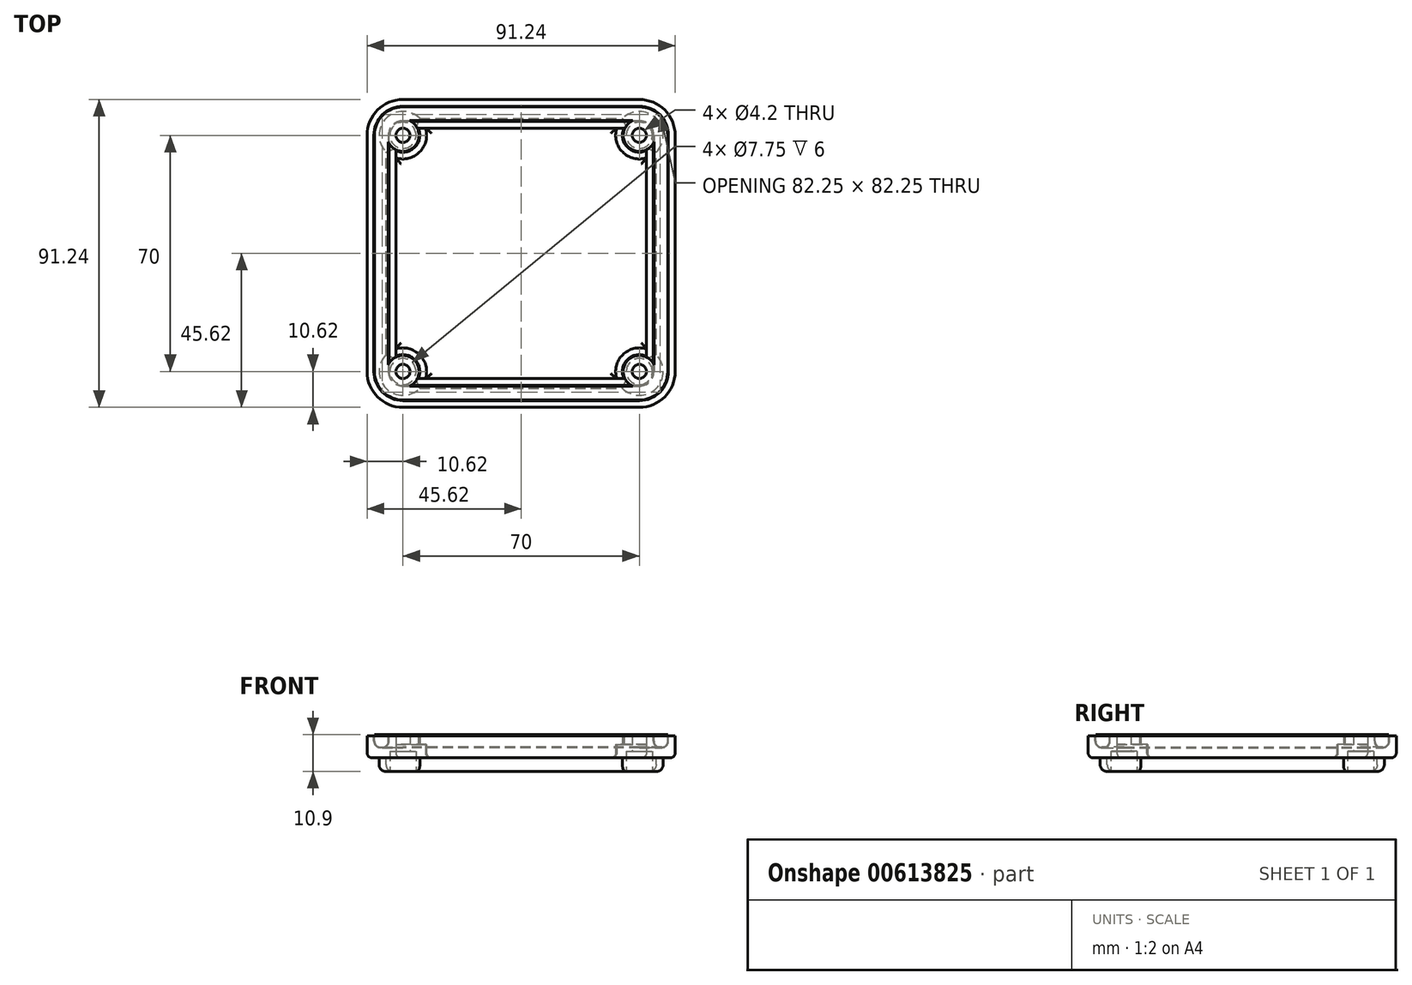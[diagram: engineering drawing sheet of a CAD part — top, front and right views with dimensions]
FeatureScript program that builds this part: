
annotation { "Feature Type Name" : "Feature", "Feature Type Description" : "" }
export const myFeature = defineFeature(function(context is Context, id is Id, definition is map)
    precondition{}
    {
        {
            var Q0;
            Q0=qCreatedBy(makeId("Top.planeOp"),FACE);
            var sketch = newSketch(context, id + "F0", { "sketchPlane" : qUnion([Q0])});
            skLineSegment(sketch, "E0.bottom", {"start": v(35, -45.63) * mm, "end": v(-35, -45.63) * mm});
            skLineSegment(sketch, "E0.top", {"start": v(35, 45.63) * mm, "end": v(-35, 45.63) * mm});
            skLineSegment(sketch, "E0.left", {"start": v(45.62, -35) * mm, "end": v(45.62, 35) * mm});
            skLineSegment(sketch, "E0.right", {"start": v(-45.62, -35) * mm, "end": v(-45.62, 35) * mm});
            skPoint(sketch, "E0.middle", {"position": v(0, 0) * mm});
            skPoint(sketch, "E1.visualSharp", {"position": v(-45.62, 45.62) * mm});
            skArc(sketch, "E1.filletArc", {"start": v(-35, 45.63) * mm, "mid": v(-42.51, 42.51) * mm, "end": v(-45.63, 35) * mm});
            skPoint(sketch, "E2.visualSharp", {"position": v(45.62, 45.63) * mm});
            skArc(sketch, "E2.filletArc", {"start": v(45.62, 35) * mm, "mid": v(42.51, 42.51) * mm, "end": v(35, 45.63) * mm});
            skPoint(sketch, "E3.visualSharp", {"position": v(45.62, -45.62) * mm});
            skArc(sketch, "E3.filletArc", {"start": v(35, -45.63) * mm, "mid": v(42.51, -42.51) * mm, "end": v(45.62, -35) * mm});
            skPoint(sketch, "E4.visualSharp", {"position": v(-45.62, -45.63) * mm});
            skArc(sketch, "E4.filletArc", {"start": v(-45.62, -35) * mm, "mid": v(-42.51, -42.51) * mm, "end": v(-35, -45.63) * mm});
            skLineSegment(sketch, "E5.bottom", {"start": v(-35, 35) * mm, "end": v(35, 35) * mm, "construction": true});
            skLineSegment(sketch, "E5.top", {"start": v(-35, -35) * mm, "end": v(35, -35) * mm, "construction": true});
            skLineSegment(sketch, "E5.left", {"start": v(-35, 35) * mm, "end": v(-35, -35) * mm, "construction": true});
            skLineSegment(sketch, "E5.right", {"start": v(35, 35) * mm, "end": v(35, -35) * mm, "construction": true});
            skCircle(sketch, "E6", {"center": v(-35, 35) * mm, "radius": 2.1 * mm});
            skCircle(sketch, "E7", {"center": v(35, 35) * mm, "radius": 2.1 * mm});
            skCircle(sketch, "E8", {"center": v(35, -35) * mm, "radius": 2.1 * mm});
            skCircle(sketch, "E9", {"center": v(-35, -35) * mm, "radius": 2.1 * mm});
            skLineSegment(sketch, "E10", {"start": v(-30.46, 37.1) * mm, "end": v(30.46, 37.1) * mm});
            skLineSegment(sketch, "E11", {"start": v(-37.1, 30.46) * mm, "end": v(-37.1, -30.46) * mm});
            skLineSegment(sketch, "E12", {"start": v(-30.46, -37.1) * mm, "end": v(30.46, -37.1) * mm});
            skLineSegment(sketch, "E13", {"start": v(37.1, -30.46) * mm, "end": v(37.1, 30.46) * mm});
            skArc(sketch, "E14", {"start": v(30.46, 37.1) * mm, "mid": v(31.46, 31.46) * mm, "end": v(37.1, 30.46) * mm});
            skArc(sketch, "E15", {"start": v(-37.1, 30.46) * mm, "mid": v(-31.46, 31.46) * mm, "end": v(-30.46, 37.1) * mm});
            skArc(sketch, "E16", {"start": v(-30.46, -37.1) * mm, "mid": v(-31.46, -31.46) * mm, "end": v(-37.1, -30.46) * mm});
            skArc(sketch, "E17", {"start": v(37.1, -30.46) * mm, "mid": v(31.46, -31.46) * mm, "end": v(30.46, -37.1) * mm});
            skPoint(sketch, "E18.orphan", {"position": v(-37.1, 35) * mm});
            skPoint(sketch, "E19.orphan", {"position": v(-35, 37.1) * mm});
            skPoint(sketch, "E20.orphan", {"position": v(37.1, 35) * mm});
            skPoint(sketch, "E21.orphan", {"position": v(37.1, -35) * mm});
            skPoint(sketch, "E22.orphan", {"position": v(35, -37.1) * mm});
            skPoint(sketch, "E23.orphan", {"position": v(-37.1, -35) * mm});
            skPoint(sketch, "E24.orphan", {"position": v(-35, -37.1) * mm});
            skSolve(sketch);
        }
        {
            var Q0;
            Q0 = qSketchRegion(id + "F0", true);
            extrude(context, id + "F1", {"entities" : qUnion([Q0]), "depth" : 6.5 * mm, "offsetDistance" : 25 * mm});
        }
        {
            var Q0;
            Q0=makeQuery(id+"F1.opExtrude","CAP_FACE",FACE,{"disambiguationData":[OSD([sQuery(id+"F0.wireOp",EDGE,"E0.bottom"),sQuery(id+"F0.wireOp",EDGE,"E0.top"),sQuery(id+"F0.wireOp",EDGE,"E0.left"),sQuery(id+"F0.wireOp",EDGE,"E0.right"),sQuery(id+"F0.wireOp",EDGE,"E1.filletArc"),sQuery(id+"F0.wireOp",EDGE,"E2.filletArc"),sQuery(id+"F0.wireOp",EDGE,"E3.filletArc"),sQuery(id+"F0.wireOp",EDGE,"E4.filletArc"),sQuery(id+"F0.wireOp",EDGE,"E6"),sQuery(id+"F0.wireOp",EDGE,"E7"),sQuery(id+"F0.wireOp",EDGE,"E8"),sQuery(id+"F0.wireOp",EDGE,"E9"),sQuery(id+"F0.wireOp",EDGE,"E10"),sQuery(id+"F0.wireOp",EDGE,"E11"),sQuery(id+"F0.wireOp",EDGE,"E12"),sQuery(id+"F0.wireOp",EDGE,"E13"),sQuery(id+"F0.wireOp",EDGE,"E14"),sQuery(id+"F0.wireOp",EDGE,"E15"),sQuery(id+"F0.wireOp",EDGE,"E16"),sQuery(id+"F0.wireOp",EDGE,"E17")])],"isStart":false});
            var sketch = newSketch(context, id + "F2", { "sketchPlane" : qUnion([Q0])});
            skArc(sketch, "E25.0", {"start": v(43.62, 35) * mm, "mid": v(41.1, 41.1) * mm, "end": v(35, 43.63) * mm});
            skLineSegment(sketch, "E25.1", {"start": v(43.62, -35) * mm, "end": v(43.62, 35) * mm});
            skLineSegment(sketch, "E25.2", {"start": v(35, 43.63) * mm, "end": v(-35, 43.63) * mm});
            skArc(sketch, "E25.3", {"start": v(35, -43.63) * mm, "mid": v(41.1, -41.1) * mm, "end": v(43.62, -35) * mm});
            skArc(sketch, "E25.4", {"start": v(-35, 43.63) * mm, "mid": v(-41.1, 41.1) * mm, "end": v(-43.63, 35) * mm});
            skLineSegment(sketch, "E25.5", {"start": v(-43.62, -35) * mm, "end": v(-43.62, 35) * mm});
            skArc(sketch, "E25.6", {"start": v(-43.62, -35) * mm, "mid": v(-41.1, -41.1) * mm, "end": v(-35, -43.63) * mm});
            skLineSegment(sketch, "E25.7", {"start": v(35, -43.63) * mm, "end": v(-35, -43.63) * mm});
            skArc(sketch, "E26.0", {"start": v(39.12, 35) * mm, "mid": v(37.92, 37.92) * mm, "end": v(35, 39.13) * mm});
            skLineSegment(sketch, "E26.1", {"start": v(39.12, -35) * mm, "end": v(39.12, 35) * mm});
            skLineSegment(sketch, "E26.2", {"start": v(35, 39.13) * mm, "end": v(-35, 39.13) * mm});
            skArc(sketch, "E26.3", {"start": v(35, -39.13) * mm, "mid": v(37.92, -37.92) * mm, "end": v(39.12, -35) * mm});
            skArc(sketch, "E26.4", {"start": v(-35, 39.13) * mm, "mid": v(-37.92, 37.92) * mm, "end": v(-39.13, 35) * mm});
            skLineSegment(sketch, "E26.5", {"start": v(-39.12, -35) * mm, "end": v(-39.12, 35) * mm});
            skArc(sketch, "E26.6", {"start": v(-39.12, -35) * mm, "mid": v(-37.92, -37.92) * mm, "end": v(-35, -39.13) * mm});
            skLineSegment(sketch, "E26.7", {"start": v(35, -39.13) * mm, "end": v(-35, -39.13) * mm});
            skSolve(sketch);
        }
        {
            var Q0;
            Q0 = qSketchRegion(id + "F2", true);
            extrude(context, id + "F3", {"entities" : qUnion([Q0]), "operationType" : NewBodyOperationType.REMOVE, "oppositeDirection" : true, "depth" : 3.5 * mm, "offsetDistance" : 25 * mm});
        }
        {
            var Q0;
            Q0=makeQuery(id+"F3.boolean.opBoolean","COPY",FACE,{"derivedFrom":makeQuery(id+"F3.opExtrude","CAP_FACE",FACE,{"disambiguationData":[OSD([sQuery(id+"F2.wireOp",EDGE,"E25.0"),sQuery(id+"F2.wireOp",EDGE,"E25.1"),sQuery(id+"F2.wireOp",EDGE,"E25.2"),sQuery(id+"F2.wireOp",EDGE,"E25.3"),sQuery(id+"F2.wireOp",EDGE,"E25.4"),sQuery(id+"F2.wireOp",EDGE,"E25.5"),sQuery(id+"F2.wireOp",EDGE,"E25.6"),sQuery(id+"F2.wireOp",EDGE,"E25.7"),sQuery(id+"F2.wireOp",EDGE,"E26.0"),sQuery(id+"F2.wireOp",EDGE,"E26.1"),sQuery(id+"F2.wireOp",EDGE,"E26.2"),sQuery(id+"F2.wireOp",EDGE,"E26.3"),sQuery(id+"F2.wireOp",EDGE,"E26.4"),sQuery(id+"F2.wireOp",EDGE,"E26.5"),sQuery(id+"F2.wireOp",EDGE,"E26.6"),sQuery(id+"F2.wireOp",EDGE,"E26.7")])],"isStart":false})});
            fillet(context, id + "F4", {"entities" : qUnion([Q0]), "radius" : 2 * mm, "tangentPropagation" : true, "allowEdgeOverflow" : false});
        }
        {
            var Q0;
            Q0=makeQuery(id+"F1.opExtrude","CAP_FACE",FACE,{"disambiguationData":[OSD([sQuery(id+"F0.wireOp",EDGE,"E0.bottom"),sQuery(id+"F0.wireOp",EDGE,"E0.top"),sQuery(id+"F0.wireOp",EDGE,"E0.left"),sQuery(id+"F0.wireOp",EDGE,"E0.right"),sQuery(id+"F0.wireOp",EDGE,"E1.filletArc"),sQuery(id+"F0.wireOp",EDGE,"E2.filletArc"),sQuery(id+"F0.wireOp",EDGE,"E3.filletArc"),sQuery(id+"F0.wireOp",EDGE,"E4.filletArc"),sQuery(id+"F0.wireOp",EDGE,"E6"),sQuery(id+"F0.wireOp",EDGE,"E7"),sQuery(id+"F0.wireOp",EDGE,"E8"),sQuery(id+"F0.wireOp",EDGE,"E9"),sQuery(id+"F0.wireOp",EDGE,"E10"),sQuery(id+"F0.wireOp",EDGE,"E11"),sQuery(id+"F0.wireOp",EDGE,"E12"),sQuery(id+"F0.wireOp",EDGE,"E13"),sQuery(id+"F0.wireOp",EDGE,"E14"),sQuery(id+"F0.wireOp",EDGE,"E15"),sQuery(id+"F0.wireOp",EDGE,"E16"),sQuery(id+"F0.wireOp",EDGE,"E17")])],"isStart":true});
            var sketch = newSketch(context, id + "F5", { "sketchPlane" : qUnion([Q0])});
            skLineSegment(sketch, "E27.bottom", {"start": v(-30, 40) * mm, "end": v(30, 40) * mm});
            skLineSegment(sketch, "E27.top", {"start": v(-30, -40) * mm, "end": v(30, -40) * mm});
            skLineSegment(sketch, "E27.left", {"start": v(-40, 30) * mm, "end": v(-40, -30) * mm});
            skLineSegment(sketch, "E27.right", {"start": v(40, 30) * mm, "end": v(40, -30) * mm});
            skPoint(sketch, "E27.middle", {"position": v(0, 0) * mm});
            skArc(sketch, "E28", {"start": v(-30, 40) * mm, "mid": v(-40, 40) * mm, "end": v(-40, 30) * mm});
            skArc(sketch, "E29", {"start": v(40, 30) * mm, "mid": v(40, 40) * mm, "end": v(30, 40) * mm});
            skArc(sketch, "E30", {"start": v(30, -40) * mm, "mid": v(40, -40) * mm, "end": v(40, -30) * mm});
            skArc(sketch, "E31", {"start": v(-40, -30) * mm, "mid": v(-40, -40) * mm, "end": v(-30, -40) * mm});
            skPoint(sketch, "E32.orphan", {"position": v(-40, -40) * mm});
            skPoint(sketch, "E33.orphan", {"position": v(40, -40) * mm});
            skPoint(sketch, "E34.orphan", {"position": v(40, 40) * mm});
            skPoint(sketch, "E35.orphan", {"position": v(-40, 40) * mm});
            skCircle(sketch, "E36.0", {"center": v(-35, 35) * mm, "radius": 2.1 * mm});
            skCircle(sketch, "E36.1", {"center": v(-35, -35) * mm, "radius": 2.1 * mm});
            skCircle(sketch, "E36.2", {"center": v(35, -35) * mm, "radius": 2.1 * mm});
            skCircle(sketch, "E36.3", {"center": v(35, 35) * mm, "radius": 2.1 * mm});
            skSolve(sketch);
        }
        {
            var Q0;
            Q0 = qSketchRegion(id + "F5", true);
            extrude(context, id + "F6", {"entities" : qUnion([Q0]), "operationType" : NewBodyOperationType.ADD, "depth" : 4 * mm, "offsetDistance" : 25 * mm});
        }
        {
            var Q0;
            Q0=makeQuery(id+"F6.opExtrude","CAP_FACE",FACE,{"disambiguationData":[OSD([sQuery(id+"F5.wireOp",EDGE,"E27.bottom"),sQuery(id+"F5.wireOp",EDGE,"E27.top"),sQuery(id+"F5.wireOp",EDGE,"E27.left"),sQuery(id+"F5.wireOp",EDGE,"E27.right"),sQuery(id+"F5.wireOp",EDGE,"E28"),sQuery(id+"F5.wireOp",EDGE,"E29"),sQuery(id+"F5.wireOp",EDGE,"E30"),sQuery(id+"F5.wireOp",EDGE,"E31"),sQuery(id+"F5.wireOp",EDGE,"E36.0"),sQuery(id+"F5.wireOp",EDGE,"E36.1"),sQuery(id+"F5.wireOp",EDGE,"E36.2"),sQuery(id+"F5.wireOp",EDGE,"E36.3")])],"isStart":true});
            var sketch = newSketch(context, id + "F7", { "sketchPlane" : qUnion([Q0])});
            skArc(sketch, "E37", {"start": v(-28.32, -37.1) * mm, "mid": v(-30.05, -30.05) * mm, "end": v(-37.1, -28.32) * mm});
            skArc(sketch, "E38", {"start": v(37.1, -28.32) * mm, "mid": v(30.05, -30.05) * mm, "end": v(28.32, -37.1) * mm});
            skArc(sketch, "E39", {"start": v(28.32, 37.1) * mm, "mid": v(30.05, 30.05) * mm, "end": v(37.1, 28.32) * mm});
            skArc(sketch, "E40", {"start": v(-37.1, 28.32) * mm, "mid": v(-30.05, 30.05) * mm, "end": v(-28.32, 37.1) * mm});
            skLineSegment(sketch, "E41.0", {"start": v(-30.46, -37.1) * mm, "end": v(-28.32, -37.1) * mm});
            skArc(sketch, "E41.1", {"start": v(37.1, -30.46) * mm, "mid": v(31.46, -31.46) * mm, "end": v(30.46, -37.1) * mm});
            skLineSegment(sketch, "E41.2", {"start": v(37.1, -30.46) * mm, "end": v(37.1, -28.32) * mm});
            skArc(sketch, "E41.3", {"start": v(30.46, 37.1) * mm, "mid": v(31.46, 31.46) * mm, "end": v(37.1, 30.46) * mm});
            skArc(sketch, "E41.4", {"start": v(-30.46, -37.1) * mm, "mid": v(-31.46, -31.46) * mm, "end": v(-37.1, -30.46) * mm});
            skLineSegment(sketch, "E41.5", {"start": v(-37.1, 30.46) * mm, "end": v(-37.1, 28.32) * mm});
            skArc(sketch, "E41.6", {"start": v(-37.1, 30.46) * mm, "mid": v(-31.46, 31.46) * mm, "end": v(-30.46, 37.1) * mm});
            skLineSegment(sketch, "E41.7", {"start": v(-30.46, 37.1) * mm, "end": v(-28.32, 37.1) * mm});
            skLineSegment(sketch, "E42.trimOffspring", {"start": v(28.32, -37.1) * mm, "end": v(30.46, -37.1) * mm});
            skLineSegment(sketch, "E43.trimOffspring", {"start": v(-37.1, -28.32) * mm, "end": v(-37.1, -30.46) * mm});
            skLineSegment(sketch, "E44.trimOffspring", {"start": v(28.32, 37.1) * mm, "end": v(30.46, 37.1) * mm});
            skLineSegment(sketch, "E45.trimOffspring", {"start": v(37.1, 28.32) * mm, "end": v(37.1, 30.46) * mm});
            skSolve(sketch);
        }
        {
            var Q0;
            Q0 = qSketchRegion(id + "F7", true);
            extrude(context, id + "F8", {"entities" : qUnion([Q0]), "operationType" : NewBodyOperationType.ADD, "depth" : 4 * mm, "offsetDistance" : 25 * mm});
        }
        {
            var Q0;
            Q0=makeQuery(id+"F6.opExtrude","CAP_FACE",FACE,{"disambiguationData":[OSD([sQuery(id+"F5.wireOp",EDGE,"E27.bottom"),sQuery(id+"F5.wireOp",EDGE,"E27.top"),sQuery(id+"F5.wireOp",EDGE,"E27.left"),sQuery(id+"F5.wireOp",EDGE,"E27.right"),sQuery(id+"F5.wireOp",EDGE,"E28"),sQuery(id+"F5.wireOp",EDGE,"E29"),sQuery(id+"F5.wireOp",EDGE,"E30"),sQuery(id+"F5.wireOp",EDGE,"E31"),sQuery(id+"F5.wireOp",EDGE,"E36.0"),sQuery(id+"F5.wireOp",EDGE,"E36.1"),sQuery(id+"F5.wireOp",EDGE,"E36.2"),sQuery(id+"F5.wireOp",EDGE,"E36.3")])],"isStart":true});
            var Q1;
            Q1=makeQuery(id+"F6.opExtrude","CAP_EDGE",EDGE,{"disambiguationData":[OSD([sQuery(id+"F5.wireOp",EDGE,"E27.bottom")])],"isStart":true});
            var Q2;
            Q2=makeQuery(id+"F6.opExtrude","CAP_EDGE",EDGE,{"disambiguationData":[OSD([sQuery(id+"F5.wireOp",EDGE,"E28")])],"isStart":true});
            var Q3;
            Q3=makeQuery(id+"F6.opExtrude","CAP_EDGE",EDGE,{"disambiguationData":[OSD([sQuery(id+"F5.wireOp",EDGE,"E27.left")])],"isStart":true});
            var Q4;
            Q4=makeQuery(id+"F6.opExtrude","CAP_EDGE",EDGE,{"disambiguationData":[OSD([sQuery(id+"F5.wireOp",EDGE,"E31")])],"isStart":true});
            var Q5;
            Q5=makeQuery(id+"F6.opExtrude","CAP_EDGE",EDGE,{"disambiguationData":[OSD([sQuery(id+"F5.wireOp",EDGE,"E27.top")])],"isStart":true});
            var Q6;
            Q6=makeQuery(id+"F6.opExtrude","CAP_EDGE",EDGE,{"disambiguationData":[OSD([sQuery(id+"F5.wireOp",EDGE,"E30")])],"isStart":true});
            var Q7;
            Q7=makeQuery(id+"F6.opExtrude","CAP_EDGE",EDGE,{"disambiguationData":[OSD([sQuery(id+"F5.wireOp",EDGE,"E27.right")])],"isStart":true});
            var Q8;
            Q8=makeQuery(id+"F6.opExtrude","CAP_EDGE",EDGE,{"disambiguationData":[OSD([sQuery(id+"F5.wireOp",EDGE,"E29")])],"isStart":true});
            var Q9;
            Q9=makeQuery(id+"F1.opExtrude","CAP_EDGE",EDGE,{"disambiguationData":[OSD([sQuery(id+"F0.wireOp",EDGE,"E4.filletArc")])],"isStart":true});
            fillet(context, id + "F9", {"entities" : qUnion([Q0, Q1, Q2, Q3, Q4, Q5, Q6, Q7, Q8, Q9]), "radius" : 1.5 * mm, "tangentPropagation" : true, "allowEdgeOverflow" : false});
        }
        {
            var Q0;
            Q0=makeQuery(id+"F6.opExtrude","CAP_FACE",FACE,{"disambiguationData":[OSD([sQuery(id+"F5.wireOp",EDGE,"E27.bottom"),sQuery(id+"F5.wireOp",EDGE,"E27.top"),sQuery(id+"F5.wireOp",EDGE,"E27.left"),sQuery(id+"F5.wireOp",EDGE,"E27.right"),sQuery(id+"F5.wireOp",EDGE,"E28"),sQuery(id+"F5.wireOp",EDGE,"E29"),sQuery(id+"F5.wireOp",EDGE,"E30"),sQuery(id+"F5.wireOp",EDGE,"E31"),sQuery(id+"F5.wireOp",EDGE,"E36.0"),sQuery(id+"F5.wireOp",EDGE,"E36.1"),sQuery(id+"F5.wireOp",EDGE,"E36.2"),sQuery(id+"F5.wireOp",EDGE,"E36.3")])],"isStart":false});
            var sketch = newSketch(context, id + "F10", { "sketchPlane" : qUnion([Q0])});
            skCircle(sketch, "E46", {"center": v(-35, 35) * mm, "radius": 3.88 * mm});
            skCircle(sketch, "E47", {"center": v(-35, -35) * mm, "radius": 3.88 * mm});
            skCircle(sketch, "E48", {"center": v(35, -35) * mm, "radius": 3.88 * mm});
            skCircle(sketch, "E49", {"center": v(35, 35) * mm, "radius": 3.88 * mm});
            skSolve(sketch);
        }
        {
            var Q0;
            Q0 = qSketchRegion(id + "F10", true);
            extrude(context, id + "F11", {"entities" : qUnion([Q0]), "operationType" : NewBodyOperationType.REMOVE, "oppositeDirection" : true, "depth" : 6 * mm, "offsetDistance" : 25 * mm});
        }
        {
            var Q0;
            Q0=makeQuery(id+"F6.opExtrude","CAP_EDGE",EDGE,{"disambiguationData":[OSD([sQuery(id+"F5.wireOp",EDGE,"E27.left")])],"isStart":false});
            var Q1;
            Q1=makeQuery(id+"F6.opExtrude","CAP_EDGE",EDGE,{"disambiguationData":[OSD([sQuery(id+"F5.wireOp",EDGE,"E28")])],"isStart":false});
            var Q2;
            Q2=makeQuery(id+"F6.opExtrude","CAP_EDGE",EDGE,{"disambiguationData":[OSD([sQuery(id+"F5.wireOp",EDGE,"E27.bottom")])],"isStart":false});
            var Q3;
            Q3=makeQuery(id+"F6.opExtrude","CAP_EDGE",EDGE,{"disambiguationData":[OSD([sQuery(id+"F5.wireOp",EDGE,"E29")])],"isStart":false});
            var Q4;
            Q4=makeQuery(id+"F6.opExtrude","CAP_EDGE",EDGE,{"disambiguationData":[OSD([sQuery(id+"F5.wireOp",EDGE,"E30")])],"isStart":false});
            var Q5;
            Q5=makeQuery(id+"F6.opExtrude","CAP_EDGE",EDGE,{"disambiguationData":[OSD([sQuery(id+"F5.wireOp",EDGE,"E27.right")])],"isStart":false});
            var Q6;
            Q6=makeQuery(id+"F6.opExtrude","CAP_EDGE",EDGE,{"disambiguationData":[OSD([sQuery(id+"F5.wireOp",EDGE,"E27.top")])],"isStart":false});
            var Q7;
            Q7=makeQuery(id+"F6.opExtrude","CAP_EDGE",EDGE,{"disambiguationData":[OSD([sQuery(id+"F5.wireOp",EDGE,"E31")])],"isStart":false});
            fillet(context, id + "F12", {"entities" : qUnion([Q0, Q1, Q2, Q3, Q4, Q5, Q6, Q7]), "radius" : 2 * mm, "tangentPropagation" : true, "allowEdgeOverflow" : false});
        }
        {
            var Q0;
            {var subQ0=sQuery(id+"F0.wireOp",EDGE,"E0.left");var subQ1=sQuery(id+"F0.wireOp",EDGE,"E4.filletArc");var subQ2=sQuery(id+"F0.wireOp",EDGE,"E3.filletArc");var subQ3=sQuery(id+"F0.wireOp",EDGE,"E2.filletArc");var subQ4=sQuery(id+"F0.wireOp",EDGE,"E1.filletArc");var subQ5=sQuery(id+"F0.wireOp",EDGE,"E0.bottom");var subQ6=sQuery(id+"F0.wireOp",EDGE,"E0.right");var subQ7=sQuery(id+"F0.wireOp",EDGE,"E0.top");Q0=makeQuery(id+"F3.boolean.opBoolean","SPLIT",FACE,{"disambiguationData":[TD([makeQuery(id+"F1.opExtrude","SWEPT_FACE",FACE,{"disambiguationData":[OSD([subQ5])]})])],"derivedFrom":makeQuery(id+"F1.opExtrude","CAP_FACE",FACE,{"disambiguationData":[OSD([subQ5,subQ7,subQ0,subQ6,subQ4,subQ3,subQ2,subQ1,sQuery(id+"F0.wireOp",EDGE,"E6"),sQuery(id+"F0.wireOp",EDGE,"E7"),sQuery(id+"F0.wireOp",EDGE,"E8"),sQuery(id+"F0.wireOp",EDGE,"E9"),sQuery(id+"F0.wireOp",EDGE,"E10"),sQuery(id+"F0.wireOp",EDGE,"E11"),sQuery(id+"F0.wireOp",EDGE,"E12"),sQuery(id+"F0.wireOp",EDGE,"E13"),sQuery(id+"F0.wireOp",EDGE,"E14"),sQuery(id+"F0.wireOp",EDGE,"E15"),sQuery(id+"F0.wireOp",EDGE,"E16"),sQuery(id+"F0.wireOp",EDGE,"E17")])],"isStart":false})});}
            var sketch = newSketch(context, id + "F13", { "sketchPlane" : qUnion([Q0])});
            skArc(sketch, "E50.0", {"start": v(-43.42, -35) * mm, "mid": v(-40.96, -40.96) * mm, "end": v(-35, -43.43) * mm});
            skLineSegment(sketch, "E50.1", {"start": v(35, -43.43) * mm, "end": v(-35, -43.43) * mm});
            skLineSegment(sketch, "E50.2", {"start": v(-43.42, -35) * mm, "end": v(-43.42, 35) * mm});
            skArc(sketch, "E50.3", {"start": v(35, -43.43) * mm, "mid": v(40.96, -40.96) * mm, "end": v(43.42, -35) * mm});
            skArc(sketch, "E50.4", {"start": v(-35, 43.43) * mm, "mid": v(-40.96, 40.96) * mm, "end": v(-43.43, 35) * mm});
            skLineSegment(sketch, "E50.5", {"start": v(35, 43.43) * mm, "end": v(-35, 43.43) * mm});
            skArc(sketch, "E50.6", {"start": v(43.42, 35) * mm, "mid": v(40.96, 40.96) * mm, "end": v(35, 43.43) * mm});
            skLineSegment(sketch, "E50.7", {"start": v(43.42, -35) * mm, "end": v(43.42, 35) * mm});
            skLineSegment(sketch, "E51.0", {"start": v(-39.32, -35) * mm, "end": v(-39.32, 35) * mm});
            skArc(sketch, "E51.1", {"start": v(-35, 39.33) * mm, "mid": v(-38.06, 38.06) * mm, "end": v(-39.33, 35) * mm});
            skArc(sketch, "E51.2", {"start": v(-39.32, -35) * mm, "mid": v(-38.06, -38.06) * mm, "end": v(-35, -39.33) * mm});
            skLineSegment(sketch, "E51.3", {"start": v(35, 39.33) * mm, "end": v(-35, 39.33) * mm});
            skLineSegment(sketch, "E51.4", {"start": v(35, -39.33) * mm, "end": v(-35, -39.33) * mm});
            skArc(sketch, "E51.5", {"start": v(35, -39.33) * mm, "mid": v(38.06, -38.06) * mm, "end": v(39.32, -35) * mm});
            skLineSegment(sketch, "E51.6", {"start": v(39.32, -35) * mm, "end": v(39.32, 35) * mm});
            skArc(sketch, "E51.7", {"start": v(39.32, 35) * mm, "mid": v(38.06, 38.06) * mm, "end": v(35, 39.33) * mm});
            skSolve(sketch);
        }
        {
            var Q0;
            Q0 = qSketchRegion(id + "F13", true);
            extrude(context, id + "F14", {"entities" : qUnion([Q0]), "oppositeDirection" : true, "depth" : 3.3 * mm, "offsetDistance" : 25 * mm, "hasSecondDirection" : true, "secondDirectionOppositeDirection" : false, "secondDirectionDepth" : 0.4 * mm});
        }
        {
            var Q0;
            Q0=makeQuery(id+"F14.opExtrude","CAP_FACE",FACE,{"disambiguationData":[OSD([sQuery(id+"F13.wireOp",EDGE,"E50.0"),sQuery(id+"F13.wireOp",EDGE,"E50.1"),sQuery(id+"F13.wireOp",EDGE,"E50.2"),sQuery(id+"F13.wireOp",EDGE,"E50.3"),sQuery(id+"F13.wireOp",EDGE,"E50.4"),sQuery(id+"F13.wireOp",EDGE,"E50.5"),sQuery(id+"F13.wireOp",EDGE,"E50.6"),sQuery(id+"F13.wireOp",EDGE,"E50.7"),sQuery(id+"F13.wireOp",EDGE,"E51.0"),sQuery(id+"F13.wireOp",EDGE,"E51.1"),sQuery(id+"F13.wireOp",EDGE,"E51.2"),sQuery(id+"F13.wireOp",EDGE,"E51.3"),sQuery(id+"F13.wireOp",EDGE,"E51.4"),sQuery(id+"F13.wireOp",EDGE,"E51.5"),sQuery(id+"F13.wireOp",EDGE,"E51.6"),sQuery(id+"F13.wireOp",EDGE,"E51.7")])],"isStart":false});
            fillet(context, id + "F15", {"entities" : qUnion([Q0]), "radius" : 1.8 * mm, "tangentPropagation" : true, "allowEdgeOverflow" : false});
        }
        {
            var Q0;
            {var subQ0=sQuery(id+"F0.wireOp",EDGE,"E15");var subQ1=sQuery(id+"F0.wireOp",EDGE,"E14");var subQ2=sQuery(id+"F0.wireOp",EDGE,"E13");var subQ3=sQuery(id+"F0.wireOp",EDGE,"E12");var subQ4=sQuery(id+"F0.wireOp",EDGE,"E11");var subQ5=sQuery(id+"F0.wireOp",EDGE,"E10");var subQ6=sQuery(id+"F0.wireOp",EDGE,"E6");var subQ7=sQuery(id+"F0.wireOp",EDGE,"E7");var subQ8=sQuery(id+"F0.wireOp",EDGE,"E8");var subQ9=sQuery(id+"F0.wireOp",EDGE,"E9");var subQ10=sQuery(id+"F0.wireOp",EDGE,"E16");var subQ11=sQuery(id+"F0.wireOp",EDGE,"E17");Q0=makeQuery(id+"F3.boolean.opBoolean","SPLIT",FACE,{"disambiguationData":[TD([makeQuery(id+"F1.opExtrude","SWEPT_FACE",FACE,{"disambiguationData":[OSD([subQ6])]})])],"derivedFrom":makeQuery(id+"F1.opExtrude","CAP_FACE",FACE,{"disambiguationData":[OSD([sQuery(id+"F0.wireOp",EDGE,"E0.bottom"),sQuery(id+"F0.wireOp",EDGE,"E0.top"),sQuery(id+"F0.wireOp",EDGE,"E0.left"),sQuery(id+"F0.wireOp",EDGE,"E0.right"),sQuery(id+"F0.wireOp",EDGE,"E1.filletArc"),sQuery(id+"F0.wireOp",EDGE,"E2.filletArc"),sQuery(id+"F0.wireOp",EDGE,"E3.filletArc"),sQuery(id+"F0.wireOp",EDGE,"E4.filletArc"),subQ6,subQ7,subQ8,subQ9,subQ5,subQ4,subQ3,subQ2,subQ1,subQ0,subQ10,subQ11])],"isStart":false})});}
            var sketch = newSketch(context, id + "F16", { "sketchPlane" : qUnion([Q0])});
            skCircle(sketch, "E52", {"center": v(35, -35) * mm, "radius": 4.75 * mm});
            skCircle(sketch, "E53", {"center": v(35, 35) * mm, "radius": 4.75 * mm});
            skCircle(sketch, "E54", {"center": v(-35, 35) * mm, "radius": 4.75 * mm});
            skCircle(sketch, "E55", {"center": v(-35, -35) * mm, "radius": 4.75 * mm});
            skCircle(sketch, "E56.0", {"center": v(-35, -35) * mm, "radius": 2.1 * mm});
            skCircle(sketch, "E56.1", {"center": v(35, -35) * mm, "radius": 2.1 * mm});
            skCircle(sketch, "E56.2", {"center": v(-35, 35) * mm, "radius": 2.1 * mm});
            skCircle(sketch, "E56.3", {"center": v(35, 35) * mm, "radius": 2.1 * mm});
            skSolve(sketch);
        }
        {
            var Q0;
            Q0 = qSketchRegion(id + "F16", true);
            var Q1;
            Q1=makeQuery(id+"F14.opExtrude","CAP_FACE",FACE,{"disambiguationData":[OSD([sQuery(id+"F13.wireOp",EDGE,"E50.0"),sQuery(id+"F13.wireOp",EDGE,"E50.1"),sQuery(id+"F13.wireOp",EDGE,"E50.2"),sQuery(id+"F13.wireOp",EDGE,"E50.3"),sQuery(id+"F13.wireOp",EDGE,"E50.4"),sQuery(id+"F13.wireOp",EDGE,"E50.5"),sQuery(id+"F13.wireOp",EDGE,"E50.6"),sQuery(id+"F13.wireOp",EDGE,"E50.7"),sQuery(id+"F13.wireOp",EDGE,"E51.0"),sQuery(id+"F13.wireOp",EDGE,"E51.1"),sQuery(id+"F13.wireOp",EDGE,"E51.2"),sQuery(id+"F13.wireOp",EDGE,"E51.3"),sQuery(id+"F13.wireOp",EDGE,"E51.4"),sQuery(id+"F13.wireOp",EDGE,"E51.5"),sQuery(id+"F13.wireOp",EDGE,"E51.6"),sQuery(id+"F13.wireOp",EDGE,"E51.7")])],"isStart":true});
            extrude(context, id + "F17", {"entities" : qUnion([Q0]), "operationType" : NewBodyOperationType.ADD, "endBound" : BoundingType.UP_TO_SURFACE, "depth" : 1.5 * mm, "endBoundEntityFace" : qUnion([Q1]), "offsetDistance" : 25 * mm});
        }
    });
